# Revit family: MADEL_GRILL_AIR RETURN_FIXED BLADES 45º_DMT
name_source: partatom
category: Terminales de aire
revit_build: Autodesk Revit 2015 (Build: 20140606_1530(x64)
units: mm (PartAtom-declared; Revit-internal decimal feet)

## types (224) — shared parameters
BIMETRICAL = http://www.bimetrical.com
BIMETRICAL Category = AirTerminal
Comentarios de tipo = The DMT series grilles are designed to be used in extractors of cold and hot air. They are mounted on walls or in false ceilings.
Descripción = MADEL_Fixed blades air return grilles
Fabricante = MADEL
Family Version = 1.0
IfcExportAs = IfcAirTerminalType
IfcExportType = IfcAirTerminalType
Imagen de tipo = <Ninguno>
Material Grill = MADEL_M9016
Review Date = 11/2016
Revit Version = Revit 2015 - English
URL = http://www.madel.com
Vmax = 3.0 m/s
Vmed = 2.3 m/s
Vmin = 1.0 m/s
b_factor = -0.128138
c_factor = -8.9597
m_factor = 1.8995
n_factor = 29.792

## per-type parameters (varying)
| type | Afree | Blade Lenght | Flujo máx. | Flujo mín. | H | H1 | H2 | Height_Connector | Kf | L | L3 | Modelo | N_Graphic lines | Nº  Blades | Product Size | Width_Connector |
| DMT-AR+CM 1200x1000 | 0.1284 m² | 1179 mm | 1,387 m³/h | 462 m³/h | 1000 mm | 985 mm | 37.9 mm | 1000 mm | 1.735604 | 1200 mm | 1185 mm | DMT-AR+CM 1200x1000 | 25 | 39 | 1200x1000 | 1200 mm |
| DMT-AR+CM 1200x900 | 0.6713 m² | 1179 mm | 7,250 m³/h | 2,417 m³/h | 900 mm | 885 mm | 36.9 mm | 900 mm | 8.885922 | 1200 mm | 1185 mm | DMT-AR+CM 1200x900 | 23 | 35 | 1200x900 | 1200 mm |
| DMT-AR+CM 1200x800 | 0.5954 m² | 1179 mm | 6,431 m³/h | 2,144 m³/h | 800 mm | 785 mm | 37.4 mm | 800 mm | 8.36743 | 1200 mm | 1185 mm | DMT-AR+CM 1200x800 | 20 | 31 | 1200x800 | 1200 mm |
| DMT-AR+CM 1200x700 | 0.5196 m² | 1179 mm | 5,611 m³/h | 1,870 m³/h | 700 mm | 685 mm | 36.1 mm | 700 mm | 7.778179 | 1200 mm | 1185 mm | DMT-AR+CM 1200x700 | 18 | 27 | 1200x700 | 1200 mm |
| DMT-AR+CM 1200x600 | 0.4437 m² | 1179 mm | 4,792 m³/h | 1,597 m³/h | 600 mm | 585 mm | 36.6 mm | 600 mm | 7.095754 | 1200 mm | 1185 mm | DMT-AR+CM 1200x600 | 15 | 23 | 1200x600 | 1200 mm |
| DMT-AR+CM 1200x500 | 0.3679 m² | 1179 mm | 3,973 m³/h | 1,324 m³/h | 500 mm | 485 mm | 34.6 mm | 500 mm | 6.285056 | 1200 mm | 1185 mm | DMT-AR+CM 1200x500 | 13 | 19 | 1200x500 | 1200 mm |
| DMT-AR+CM 1200x450 | 0.3299 m² | 1179 mm | 3,563 m³/h | 1,188 m³/h | 450 mm  [stored 1.47638 ft] | 435 mm | 36.3 mm | 450 mm  [stored 1.47638 ft] | 5.814512 | 1200 mm | 1185 mm | DMT-AR+CM 1200x450 | 11 | 17 | 1200x450 | 1200 mm |
| DMT-AR+CM 1200x400 | 0.2920 m² | 1179 mm | 3,153 m³/h | 1,051 m³/h | 400 mm  [stored 1.31234 ft] | 385 mm | 35 mm  [stored 0.114829 ft] | 400 mm  [stored 1.31234 ft] | 5.286433 | 1200 mm | 1185 mm | DMT-AR+CM 1200x400 | 10 | 15 | 1200x400 | 1200 mm |
| DMT-AR+CM 1200x350 | 0.2541 m² | 1179 mm | 2,744 m³/h | 915 m³/h | 350 mm  [stored 1.14829 ft] | 335 mm | 33.5 mm | 350 mm  [stored 1.14829 ft] | 4.684763 | 1200 mm | 1185 mm | DMT-AR+CM 1200x350 | 9 | 13 | 1200x350 | 1200 mm |
| DMT-AR+CM 1200x300 | 0.2161 m² | 1179 mm | 2,334 m³/h | 778 m³/h | 300 mm | 285 mm  [stored 0.935039 ft] | 31.7 mm | 300 mm | 3.985618 | 1200 mm | 1185 mm | DMT-AR+CM 1200x300 | 8 | 11 | 1200x300 | 1200 mm |
| DMT-AR+CM 1200x250 | 0.1782 m² | 1179 mm | 1,924 m³/h | 641 m³/h | 250 mm  [stored 0.82021 ft] | 235 mm  [stored 0.770997 ft] | 33.6 mm | 250 mm  [stored 0.82021 ft] | 3.15119 | 1200 mm | 1185 mm | DMT-AR+CM 1200x250 | 6 | 9 | 1200x250 | 1200 mm |
| DMT-AR+CM 1200x200 | 0.1403 m² | 1179 mm | 1,515 m³/h | 505 m³/h | 200 mm  [stored 0.656168 ft] | 185 mm  [stored 0.606955 ft] | 30.8 mm | 200 mm  [stored 0.656168 ft] | 2.116257 | 1200 mm | 1185 mm | DMT-AR+CM 1200x200 | 5 | 7 | 1200x200 | 1200 mm |
| DMT-AR+CM 1200x150 | 0.1023 m² | 1179 mm | 1,105 m³/h | 368 m³/h | 150 mm | 135 mm  [stored 0.442913 ft] | 27 mm  [stored 0.0885827 ft] | 150 mm | 0.752929 | 1200 mm | 1185 mm | DMT-AR+CM 1200x150 | 4 | 5 | 1200x150 | 1200 mm |
| DMT-AR+CM 1200x100 | 0.0644 m² | 1179 mm | 695 m³/h | 232 m³/h | 100 mm  [stored 0.328084 ft] | 85 mm  [stored 0.278871 ft] | 21.3 mm | 100 mm  [stored 0.328084 ft] | -1.249544 | 1200 mm | 1185 mm | DMT-AR+CM 1200x100 | 3 | 3 | 1200x100 | 1200 mm |
| DMT-AR+CM 1100x1000 | 0.6841 m² | 1079 mm | 7,388 m³/h | 2,463 m³/h | 1000 mm | 985 mm | 37.9 mm | 1000 mm | 8.967505 | 1100 mm | 1085 mm | DMT-AR+CM 1100x1000 | 25 | 39 | 1100x1000 | 1100 mm |
| DMT-AR+CM 1100x900 | 0.6146 m² | 1079 mm | 6,638 m³/h | 2,213 m³/h | 900 mm | 885 mm | 36.9 mm | 900 mm | 8.504605 | 1100 mm | 1085 mm | DMT-AR+CM 1100x900 | 23 | 35 | 1100x900 | 1100 mm |
| DMT-AR+CM 1100x800 | 0.5452 m² | 1079 mm | 5,888 m³/h | 1,963 m³/h | 800 mm | 785 mm | 37.4 mm | 800 mm | 7.986136 | 1100 mm | 1085 mm | DMT-AR+CM 1100x800 | 20 | 31 | 1100x800 | 1100 mm |
| DMT-AR+CM 1100x700 | 0.4757 m² | 1079 mm | 5,138 m³/h | 1,713 m³/h | 700 mm | 685 mm | 36.1 mm | 700 mm | 7.396913 | 1100 mm | 1085 mm | DMT-AR+CM 1100x700 | 18 | 27 | 1100x700 | 1100 mm |
| DMT-AR+CM 1100x600 | 0.4063 m² | 1079 mm | 4,388 m³/h | 1,463 m³/h | 600 mm | 585 mm | 36.6 mm | 600 mm | 6.714527 | 1100 mm | 1085 mm | DMT-AR+CM 1100x600 | 15 | 23 | 1100x600 | 1100 mm |
| DMT-AR+CM 1100x500 | 0.3368 m² | 1079 mm | 3,638 m³/h | 1,213 m³/h | 500 mm | 485 mm | 34.6 mm | 500 mm | 5.903883 | 1100 mm | 1085 mm | DMT-AR+CM 1100x500 | 13 | 19 | 1100x500 | 1100 mm |
| DMT-AR+CM 1100x450 | 0.3021 m² | 1079 mm | 3,262 m³/h | 1,087 m³/h | 450 mm  [stored 1.47638 ft] | 435 mm | 36.3 mm | 450 mm  [stored 1.47638 ft] | 5.433377 | 1100 mm | 1085 mm | DMT-AR+CM 1100x450 | 11 | 17 | 1100x450 | 1100 mm |
| DMT-AR+CM 1100x400 | 0.2674 m² | 1079 mm | 2,887 m³/h | 962 m³/h | 400 mm  [stored 1.31234 ft] | 385 mm | 35 mm  [stored 0.114829 ft] | 400 mm  [stored 1.31234 ft] | 4.905344 | 1100 mm | 1085 mm | DMT-AR+CM 1100x400 | 10 | 15 | 1100x400 | 1100 mm |
| DMT-AR+CM 1100x350 | 0.2326 m² | 1079 mm | 2,512 m³/h | 837 m³/h | 350 mm  [stored 1.14829 ft] | 335 mm | 33.5 mm | 350 mm  [stored 1.14829 ft] | 4.303734 | 1100 mm | 1085 mm | DMT-AR+CM 1100x350 | 9 | 13 | 1100x350 | 1100 mm |
| DMT-AR+CM 1100x300 | 0.1979 m² | 1079 mm | 2,137 m³/h | 712 m³/h | 300 mm | 285 mm  [stored 0.935039 ft] | 31.7 mm | 300 mm | 3.60467 | 1100 mm | 1085 mm | DMT-AR+CM 1100x300 | 8 | 11 | 1100x300 | 1100 mm |
| DMT-AR+CM 1100x250 | 0.1632 m² | 1079 mm | 1,762 m³/h | 587 m³/h | 250 mm  [stored 0.82021 ft] | 235 mm  [stored 0.770997 ft] | 33.6 mm | 250 mm  [stored 0.82021 ft] | 2.770358 | 1100 mm | 1085 mm | DMT-AR+CM 1100x250 | 6 | 9 | 1100x250 | 1100 mm |
| DMT-AR+CM 1100x200 | 0.1284 m² | 1079 mm | 1,387 m³/h | 462 m³/h | 200 mm  [stored 0.656168 ft] | 185 mm  [stored 0.606955 ft] | 30.8 mm | 200 mm  [stored 0.656168 ft] | 1.735604 | 1100 mm | 1085 mm | DMT-AR+CM 1100x200 | 5 | 7 | 1100x200 | 1100 mm |
| DMT-AR+CM 1100x150 | 0.0937 m² | 1079 mm | 1,012 m³/h | 337 m³/h | 150 mm | 135 mm  [stored 0.442913 ft] | 27 mm  [stored 0.0885827 ft] | 150 mm | 0.372587 | 1100 mm | 1085 mm | DMT-AR+CM 1100x150 | 4 | 5 | 1100x150 | 1100 mm |
| DMT-AR+CM 1100x100 | 0.0590 m² | 1079 mm | 637 m³/h | 212 m³/h | 100 mm  [stored 0.328084 ft] | 85 mm  [stored 0.278871 ft] | 21.3 mm | 100 mm  [stored 0.328084 ft] | -1.629207 | 1100 mm | 1085 mm | DMT-AR+CM 1100x100 | 3 | 3 | 1100x100 | 1100 mm |
| DMT-AR+CM 1000x1000 | 0.6210 m² | 979 mm | 6,707 m³/h | 2,236 m³/h | 1000 mm | 985 mm | 37.9 mm | 1000 mm | 8.549255 | 1000 mm | 985 mm | DMT-AR+CM 1000x1000 | 25 | 39 | 1000x1000 | 1000 mm |
| DMT-AR+CM 1000x900 | 0.5580 m² | 979 mm | 6,026 m³/h | 2,009 m³/h | 900 mm | 885 mm | 36.9 mm | 900 mm | 8.086376 | 1000 mm | 985 mm | DMT-AR+CM 1000x900 | 23 | 35 | 1000x900 | 1000 mm |
| DMT-AR+CM 1000x800 | 0.4949 m² | 979 mm | 5,345 m³/h | 1,782 m³/h | 800 mm | 785 mm | 37.4 mm | 800 mm | 7.567934 | 1000 mm | 985 mm | DMT-AR+CM 1000x800 | 20 | 31 | 1000x800 | 1000 mm |
| DMT-AR+CM 1000x700 | 0.4319 m² | 979 mm | 4,664 m³/h | 1,555 m³/h | 700 mm | 685 mm | 36.1 mm | 700 mm | 6.978746 | 1000 mm | 985 mm | DMT-AR+CM 1000x700 | 18 | 27 | 1000x700 | 1000 mm |
| DMT-AR+CM 1000x600 | 0.3688 m² | 979 mm | 3,983 m³/h | 1,328 m³/h | 600 mm | 585 mm | 36.6 mm | 600 mm | 6.296407 | 1000 mm | 985 mm | DMT-AR+CM 1000x600 | 15 | 23 | 1000x600 | 1000 mm |
| DMT-AR+CM 1000x500 | 0.3058 m² | 979 mm | 3,302 m³/h | 1,101 m³/h | 500 mm | 485 mm | 34.6 mm | 500 mm | 5.485829 | 1000 mm | 985 mm | DMT-AR+CM 1000x500 | 13 | 19 | 1000x500 | 1000 mm |
| DMT-AR+CM 1000x450 | 0.2742 m² | 979 mm | 2,962 m³/h | 987 m³/h | 450 mm  [stored 1.47638 ft] | 435 mm | 36.3 mm | 450 mm  [stored 1.47638 ft] | 5.015366 | 1000 mm | 985 mm | DMT-AR+CM 1000x450 | 11 | 17 | 1000x450 | 1000 mm |
| DMT-AR+CM 1000x400 | 0.2427 m² | 979 mm | 2,621 m³/h | 874 m³/h | 400 mm  [stored 1.31234 ft] | 385 mm | 35 mm  [stored 0.114829 ft] | 400 mm  [stored 1.31234 ft] | 4.48739 | 1000 mm | 985 mm | DMT-AR+CM 1000x400 | 10 | 15 | 1000x400 | 1000 mm |
| DMT-AR+CM 1000x350 | 0.2112 m² | 979 mm | 2,281 m³/h | 760 m³/h | 350 mm  [stored 1.14829 ft] | 335 mm | 33.5 mm | 350 mm  [stored 1.14829 ft] | 3.885852 | 1000 mm | 985 mm | DMT-AR+CM 1000x350 | 9 | 13 | 1000x350 | 1000 mm |
| DMT-AR+CM 1000x300 | 0.1797 m² | 979 mm | 1,940 m³/h | 647 m³/h | 300 mm | 285 mm  [stored 0.935039 ft] | 31.7 mm | 300 mm | 3.186886 | 1000 mm | 985 mm | DMT-AR+CM 1000x300 | 8 | 11 | 1000x300 | 1000 mm |
| DMT-AR+CM 1000x250 | 0.1481 m² | 979 mm | 1,600 m³/h | 533 m³/h | 250 mm  [stored 0.82021 ft] | 235 mm  [stored 0.770997 ft] | 33.6 mm | 250 mm  [stored 0.82021 ft] | 2.352714 | 1000 mm | 985 mm | DMT-AR+CM 1000x250 | 6 | 9 | 1000x250 | 1000 mm |
| DMT-AR+CM 1000x200 | 0.1166 m² | 979 mm | 1,259 m³/h | 420 m³/h | 200 mm  [stored 0.656168 ft] | 185 mm  [stored 0.606955 ft] | 30.8 mm | 200 mm  [stored 0.656168 ft] | 1.318174 | 1000 mm | 985 mm | DMT-AR+CM 1000x200 | 5 | 7 | 1000x200 | 1000 mm |
| DMT-AR+CM 1000x150 | 0.0851 m² | 979 mm | 919 m³/h | 306 m³/h | 150 mm | 135 mm  [stored 0.442913 ft] | 27 mm  [stored 0.0885827 ft] | 150 mm | -0.044469 | 1000 mm | 985 mm | DMT-AR+CM 1000x150 | 4 | 5 | 1000x150 | 1000 mm |
| DMT-AR+CM 1000x100 | 0.0536 m² | 979 mm | 579 m³/h | 193 m³/h | 100 mm  [stored 0.328084 ft] | 85 mm  [stored 0.278871 ft] | 21.3 mm | 100 mm  [stored 0.328084 ft] | -2.045448 | 1000 mm | 985 mm | DMT-AR+CM 1000x100 | 3 | 3 | 1000x100 | 1000 mm |
| EMT-AR+CM 1000x900 | 0.5579 m² | 879 mm | 6,026 m³/h | 2,009 m³/h | 1000 mm | 985 mm | 37.9 mm | 1000 mm | 8.086169 | 900 mm | 885 mm | EMT-AR+CM 1000x900 | 25 | 39 | 900x1000 | 900 mm |
| DMT-AR+CM 900x900 | 0.5013 m² | 879 mm | 5,414 m³/h | 1,805 m³/h | 900 mm | 885 mm | 36.9 mm | 900 mm | 7.623316 | 900 mm | 885 mm | DMT-AR+CM 900x900 | 23 | 35 | 900x900 | 900 mm |
| DMT-AR+CM 900x800 | 0.4447 m² | 879 mm | 4,802 m³/h | 1,601 m³/h | 800 mm | 785 mm | 37.4 mm | 800 mm | 7.104907 | 900 mm | 885 mm | DMT-AR+CM 900x800 | 20 | 31 | 900x800 | 900 mm |
| DMT-AR+CM 900x700 | 0.3880 m² | 879 mm | 4,191 m³/h | 1,397 m³/h | 700 mm | 685 mm | 36.1 mm | 700 mm | 6.515761 | 900 mm | 885 mm | DMT-AR+CM 900x700 | 18 | 27 | 900x700 | 900 mm |
| DMT-AR+CM 900x600 | 0.3314 m² | 879 mm | 3,579 m³/h | 1,193 m³/h | 600 mm | 585 mm | 36.6 mm | 600 mm | 5.833479 | 900 mm | 885 mm | DMT-AR+CM 900x600 | 15 | 23 | 900x600 | 900 mm |
| DMT-AR+CM 900x500 | 0.2747 m² | 879 mm | 2,967 m³/h | 989 m³/h | 500 mm | 485 mm | 34.6 mm | 500 mm | 5.022982 | 900 mm | 885 mm | DMT-AR+CM 900x500 | 13 | 19 | 900x500 | 900 mm |
| DMT-AR+CM 900x450 | 0.2464 m² | 879 mm | 2,661 m³/h | 887 m³/h | 450 mm  [stored 1.47638 ft] | 435 mm | 36.3 mm | 450 mm  [stored 1.47638 ft] | 4.552574 | 900 mm | 885 mm | DMT-AR+CM 900x450 | 11 | 17 | 900x450 | 900 mm |
| DMT-AR+CM 900x400 | 0.2181 m² | 879 mm | 2,355 m³/h | 785 m³/h | 400 mm  [stored 1.31234 ft] | 385 mm | 35 mm  [stored 0.114829 ft] | 400 mm  [stored 1.31234 ft] | 4.024666 | 900 mm | 885 mm | DMT-AR+CM 900x400 | 10 | 15 | 900x400 | 900 mm |
| DMT-AR+CM 900x350 | 0.1898 m² | 879 mm | 2,049 m³/h | 683 m³/h | 350 mm  [stored 1.14829 ft] | 335 mm | 33.5 mm | 350 mm  [stored 1.14829 ft] | 3.423217 | 900 mm | 885 mm | DMT-AR+CM 900x350 | 9 | 13 | 900x350 | 900 mm |
| DMT-AR+CM 900x300 | 0.1614 m² | 879 mm | 1,744 m³/h | 581 m³/h | 300 mm | 285 mm  [stored 0.935039 ft] | 31.7 mm | 300 mm | 2.724371 | 900 mm | 885 mm | DMT-AR+CM 900x300 | 8 | 11 | 900x300 | 900 mm |
| DMT-AR+CM 900x250 | 0.1331 m² | 879 mm | 1,438 m³/h | 479 m³/h | 250 mm  [stored 0.82021 ft] | 235 mm  [stored 0.770997 ft] | 33.6 mm | 250 mm  [stored 0.82021 ft] | 1.89037 | 900 mm | 885 mm | DMT-AR+CM 900x250 | 6 | 9 | 900x250 | 900 mm |
| DMT-AR+CM 900x200 | 0.1048 m² | 879 mm | 1,132 m³/h | 377 m³/h | 200 mm  [stored 0.656168 ft] | 185 mm  [stored 0.606955 ft] | 30.8 mm | 200 mm  [stored 0.656168 ft] | 0.856094 | 900 mm | 885 mm | DMT-AR+CM 900x200 | 5 | 7 | 900x200 | 900 mm |
| DMT-AR+CM 900x150 | 0.0765 m² | 879 mm | 826 m³/h | 275 m³/h | 150 mm | 135 mm  [stored 0.442913 ft] | 27 mm  [stored 0.0885827 ft] | 150 mm | -0.50609 | 900 mm | 885 mm | DMT-AR+CM 900x150 | 4 | 5 | 900x150 | 900 mm |
| DMT-AR+CM 900x100 | 0.0482 m² | 879 mm | 520 m³/h | 173 m³/h | 100 mm  [stored 0.328084 ft] | 85 mm  [stored 0.278871 ft] | 21.3 mm | 100 mm  [stored 0.328084 ft] | -2.506071 | 900 mm | 885 mm | DMT-AR+CM 900x100 | 3 | 3 | 900x100 | 900 mm |
| EMT-AR+CM 1000x800 | 0.4949 m² | 779 mm | 5,345 m³/h | 1,782 m³/h | 1000 mm | 985 mm | 37.9 mm | 1000 mm | 7.567467 | 800 mm | 785 mm | EMT-AR+CM 1000x800 | 25 | 39 | 800x1000 | 800 mm |
| EMT-AR+CM 900x800 | 0.4446 m² | 779 mm | 4,802 m³/h | 1,601 m³/h | 900 mm | 885 mm | 36.9 mm | 900 mm | 7.104647 | 800 mm | 785 mm | EMT-AR+CM 900x800 | 23 | 35 | 800x900 | 800 mm |
| DMT-AR+CM 800x800 | 0.3944 m² | 779 mm | 4,259 m³/h | 1,420 m³/h | 800 mm | 785 mm | 37.4 mm | 800 mm | 6.586279 | 800 mm | 785 mm | DMT-AR+CM 800x800 | 20 | 31 | 800x800 | 800 mm |
| DMT-AR+CM 800x700 | 0.3442 m² | 779 mm | 3,717 m³/h | 1,239 m³/h | 700 mm | 685 mm | 36.1 mm | 700 mm | 5.997187 | 800 mm | 785 mm | DMT-AR+CM 800x700 | 18 | 27 | 800x700 | 800 mm |
| DMT-AR+CM 800x600 | 0.2939 m² | 779 mm | 3,174 m³/h | 1,058 m³/h | 600 mm | 585 mm | 36.6 mm | 600 mm | 5.314977 | 800 mm | 785 mm | DMT-AR+CM 800x600 | 15 | 23 | 800x600 | 800 mm |
| DMT-AR+CM 800x500 | 0.2437 m² | 779 mm | 2,632 m³/h | 877 m³/h | 500 mm | 485 mm | 34.6 mm | 500 mm | 4.504581 | 800 mm | 785 mm | DMT-AR+CM 800x500 | 13 | 19 | 800x500 | 800 mm |
| DMT-AR+CM 800x450 | 0.2186 m² | 779 mm | 2,361 m³/h | 787 m³/h | 450 mm  [stored 1.47638 ft] | 435 mm | 36.3 mm | 450 mm  [stored 1.47638 ft] | 4.034241 | 800 mm | 785 mm | DMT-AR+CM 800x450 | 11 | 17 | 800x450 | 800 mm |
| DMT-AR+CM 800x400 | 0.1934 m² | 779 mm | 2,089 m³/h | 696 m³/h | 400 mm  [stored 1.31234 ft] | 385 mm | 35 mm  [stored 0.114829 ft] | 400 mm  [stored 1.31234 ft] | 3.506418 | 800 mm | 785 mm | DMT-AR+CM 800x400 | 10 | 15 | 800x400 | 800 mm |
| DMT-AR+CM 800x350 | 0.1683 m² | 779 mm | 1,818 m³/h | 606 m³/h | 350 mm  [stored 1.14829 ft] | 335 mm | 33.5 mm | 350 mm  [stored 1.14829 ft] | 2.905081 | 800 mm | 785 mm | DMT-AR+CM 800x350 | 9 | 13 | 800x350 | 800 mm |
| DMT-AR+CM 800x300 | 0.1432 m² | 779 mm | 1,547 m³/h | 516 m³/h | 300 mm | 285 mm  [stored 0.935039 ft] | 31.7 mm | 300 mm | 2.206385 | 800 mm | 785 mm | DMT-AR+CM 800x300 | 8 | 11 | 800x300 | 800 mm |
| DMT-AR+CM 800x250 | 0.1181 m² | 779 mm | 1,275 m³/h | 425 m³/h | 250 mm  [stored 0.82021 ft] | 235 mm  [stored 0.770997 ft] | 33.6 mm | 250 mm  [stored 0.82021 ft] | 1.372599 | 800 mm | 785 mm | DMT-AR+CM 800x250 | 6 | 9 | 800x250 | 800 mm |
| DMT-AR+CM 800x200 | 0.0930 m² | 779 mm | 1,004 m³/h | 335 m³/h | 200 mm  [stored 0.656168 ft] | 185 mm  [stored 0.606955 ft] | 30.8 mm | 200 mm  [stored 0.656168 ft] | 0.338653 | 800 mm | 785 mm | DMT-AR+CM 800x200 | 5 | 7 | 800x200 | 800 mm |
| DMT-AR+CM 800x150 | 0.0679 m² | 779 mm | 733 m³/h | 244 m³/h | 150 mm | 135 mm  [stored 0.442913 ft] | 27 mm  [stored 0.0885827 ft] | 150 mm | -1.022955 | 800 mm | 785 mm | DMT-AR+CM 800x150 | 4 | 5 | 800x150 | 800 mm |
| DMT-AR+CM 800x100 | 0.0427 m² | 779 mm | 462 m³/h | 154 m³/h | 100 mm  [stored 0.328084 ft] | 85 mm  [stored 0.278871 ft] | 21.3 mm | 100 mm  [stored 0.328084 ft] | -3.021685 | 800 mm | 785 mm | DMT-AR+CM 800x100 | 3 | 3 | 800x100 | 800 mm |
| EMT-AR+CM 1000x700 | 0.4318 m² | 679 mm | 4,663 m³/h | 1,554 m³/h | 1000 mm | 985 mm | 37.9 mm | 1000 mm | 6.977943 | 700 mm | 685 mm | EMT-AR+CM 1000x700 | 25 | 39 | 700x1000 | 700 mm |
| EMT-AR+CM 900x700 | 0.3880 m² | 679 mm | 4,190 m³/h | 1,397 m³/h | 900 mm | 885 mm | 36.9 mm | 900 mm | 6.515166 | 700 mm | 685 mm | EMT-AR+CM 900x700 | 23 | 35 | 700x900 | 700 mm |
| EMT-AR+CM 800x700 | 0.3441 m² | 679 mm | 3,717 m³/h | 1,239 m³/h | 800 mm | 785 mm | 37.4 mm | 800 mm | 5.996851 | 700 mm | 685 mm | EMT-AR+CM 800x700 | 20 | 31 | 700x800 | 700 mm |
| DMT-AR+CM 700x700 | 0.3003 m² | 679 mm | 3,243 m³/h | 1,081 m³/h | 700 mm | 685 mm | 36.1 mm | 700 mm | 5.407828 | 700 mm | 685 mm | DMT-AR+CM 700x700 | 18 | 27 | 700x700 | 700 mm |
| DMT-AR+CM 700x600 | 0.2565 m² | 679 mm | 2,770 m³/h | 923 m³/h | 600 mm | 585 mm | 36.6 mm | 600 mm | 4.725711 | 700 mm | 685 mm | DMT-AR+CM 700x600 | 15 | 23 | 700x600 | 700 mm |
| DMT-AR+CM 700x500 | 0.2126 m² | 679 mm | 2,297 m³/h | 766 m³/h | 500 mm | 485 mm | 34.6 mm | 500 mm | 3.915446 | 700 mm | 685 mm | DMT-AR+CM 700x500 | 13 | 19 | 700x500 | 700 mm |
| DMT-AR+CM 700x450 | 0.1907 m² | 679 mm | 2,060 m³/h | 687 m³/h | 450 mm  [stored 1.47638 ft] | 435 mm | 36.3 mm | 450 mm  [stored 1.47638 ft] | 3.445194 | 700 mm | 685 mm | DMT-AR+CM 700x450 | 11 | 17 | 700x450 | 700 mm |
| DMT-AR+CM 700x400 | 0.1688 m² | 679 mm | 1,823 m³/h | 608 m³/h | 400 mm  [stored 1.31234 ft] | 385 mm | 35 mm  [stored 0.114829 ft] | 400 mm  [stored 1.31234 ft] | 2.917482 | 700 mm | 685 mm | DMT-AR+CM 700x400 | 10 | 15 | 700x400 | 700 mm |
| DMT-AR+CM 700x350 | 0.1469 m² | 679 mm | 1,587 m³/h | 529 m³/h | 350 mm  [stored 1.14829 ft] | 335 mm | 33.5 mm | 350 mm  [stored 1.14829 ft] | 2.316289 | 700 mm | 685 mm | DMT-AR+CM 700x350 | 9 | 13 | 700x350 | 700 mm |
| DMT-AR+CM 700x300 | 0.1250 m² | 679 mm | 1,350 m³/h | 450 m³/h | 300 mm | 285 mm  [stored 0.935039 ft] | 31.7 mm | 300 mm | 1.617787 | 700 mm | 685 mm | DMT-AR+CM 700x300 | 8 | 11 | 700x300 | 700 mm |
| DMT-AR+CM 700x250 | 0.1031 m² | 679 mm | 1,113 m³/h | 371 m³/h | 250 mm  [stored 0.82021 ft] | 235 mm  [stored 0.770997 ft] | 33.6 mm | 250 mm  [stored 0.82021 ft] | 0.784278 | 700 mm | 685 mm | DMT-AR+CM 700x250 | 6 | 9 | 700x250 | 700 mm |
| DMT-AR+CM 700x200 | 0.0812 m² | 679 mm | 876 m³/h | 292 m³/h | 200 mm  [stored 0.656168 ft] | 185 mm  [stored 0.606955 ft] | 30.8 mm | 200 mm  [stored 0.656168 ft] | -0.24924 | 700 mm | 685 mm | DMT-AR+CM 700x200 | 5 | 7 | 700x200 | 700 mm |
| DMT-AR+CM 700x150 | 0.0592 m² | 679 mm | 640 m³/h | 213 m³/h | 150 mm | 135 mm  [stored 0.442913 ft] | 27 mm  [stored 0.0885827 ft] | 150 mm | -1.610107 | 700 mm | 685 mm | DMT-AR+CM 700x150 | 4 | 5 | 700x150 | 700 mm |
| DMT-AR+CM 700x100 | 0.0373 m² | 679 mm | 403 m³/h | 134 m³/h | 100 mm  [stored 0.328084 ft] | 85 mm  [stored 0.278871 ft] | 21.3 mm | 100 mm  [stored 0.328084 ft] | -3.607221 | 700 mm | 685 mm | DMT-AR+CM 700x100 | 3 | 3 | 700x100 | 700 mm |
| EMT-AR+CM 1000x600 | 0.3687 m² | 579 mm | 3,982 m³/h | 1,327 m³/h | 1000 mm | 985 mm | 37.9 mm | 1000 mm | 6.295153 | 600 mm | 585 mm | EMT-AR+CM 1000x600 | 25 | 39 | 600x1000 | 600 mm |
| EMT-AR+CM 900x600 | 0.3313 m² | 579 mm | 3,578 m³/h | 1,193 m³/h | 900 mm | 885 mm | 36.9 mm | 900 mm | 5.832433 | 600 mm | 585 mm | EMT-AR+CM 900x600 | 23 | 35 | 600x900 | 600 mm |
| EMT-AR+CM 800x600 | 0.2939 m² | 579 mm | 3,174 m³/h | 1,058 m³/h | 800 mm | 785 mm | 37.4 mm | 800 mm | 5.31419 | 600 mm | 585 mm | EMT-AR+CM 800x600 | 20 | 31 | 600x800 | 600 mm |
| EMT-AR+CM 700x600 | 0.2564 m² | 579 mm | 2,770 m³/h | 923 m³/h | 700 mm | 685 mm | 36.1 mm | 700 mm | 4.72526 | 600 mm | 585 mm | EMT-AR+CM 700x600 | 18 | 27 | 600x700 | 600 mm |
| DMT-AR+CM 600x600 | 0.2190 m² | 579 mm | 2,365 m³/h | 788 m³/h | 600 mm | 585 mm | 36.6 mm | 600 mm | 4.043267 | 600 mm | 585 mm | DMT-AR+CM 600x600 | 15 | 23 | 600x600 | 600 mm |
| DMT-AR+CM 600x500 | 0.1816 m² | 579 mm | 1,961 m³/h | 654 m³/h | 500 mm | 485 mm | 34.6 mm | 500 mm | 3.233178 | 600 mm | 585 mm | DMT-AR+CM 600x500 | 13 | 19 | 600x500 | 600 mm |
| DMT-AR+CM 600x450 | 0.1629 m² | 579 mm | 1,759 m³/h | 586 m³/h | 450 mm  [stored 1.47638 ft] | 435 mm | 36.3 mm | 450 mm  [stored 1.47638 ft] | 2.763044 | 600 mm | 585 mm | DMT-AR+CM 600x450 | 11 | 17 | 600x450 | 600 mm |
| DMT-AR+CM 600x400 | 0.1442 m² | 579 mm | 1,557 m³/h | 519 m³/h | 400 mm  [stored 1.31234 ft] | 385 mm | 35 mm  [stored 0.114829 ft] | 400 mm  [stored 1.31234 ft] | 2.235481 | 600 mm | 585 mm | DMT-AR+CM 600x400 | 10 | 15 | 600x400 | 600 mm |
| DMT-AR+CM 600x350 | 0.1255 m² | 579 mm | 1,355 m³/h | 452 m³/h | 350 mm  [stored 1.14829 ft] | 335 mm | 33.5 mm | 350 mm  [stored 1.14829 ft] | 1.634481 | 600 mm | 585 mm | DMT-AR+CM 600x350 | 9 | 13 | 600x350 | 600 mm |
| DMT-AR+CM 600x300 | 0.1068 m² | 579 mm | 1,153 m³/h | 384 m³/h | 300 mm | 285 mm  [stored 0.935039 ft] | 31.7 mm | 300 mm | 0.93624 | 600 mm | 585 mm | DMT-AR+CM 600x300 | 8 | 11 | 600x300 | 600 mm |
| DMT-AR+CM 600x250 | 0.0880 m² | 579 mm | 951 m³/h | 317 m³/h | 250 mm  [stored 0.82021 ft] | 235 mm  [stored 0.770997 ft] | 33.6 mm | 250 mm  [stored 0.82021 ft] | 0.103103 | 600 mm | 585 mm | DMT-AR+CM 600x250 | 6 | 9 | 600x250 | 600 mm |
| DMT-AR+CM 600x200 | 0.0693 m² | 579 mm | 749 m³/h | 250 m³/h | 200 mm  [stored 0.656168 ft] | 185 mm  [stored 0.606955 ft] | 30.8 mm | 200 mm  [stored 0.656168 ft] | -0.929843 | 600 mm | 585 mm | DMT-AR+CM 600x200 | 5 | 7 | 600x200 | 600 mm |
| DMT-AR+CM 600x150 | 0.0506 m² | 579 mm | 547 m³/h | 182 m³/h | 150 mm | 135 mm  [stored 0.442913 ft] | 27 mm  [stored 0.0885827 ft] | 150 mm | -2.289714 | 600 mm | 585 mm | DMT-AR+CM 600x150 | 4 | 5 | 600x150 | 600 mm |
| DMT-AR+CM 600x100 | 0.0319 m² | 579 mm | 345 m³/h | 115 m³/h | 100 mm  [stored 0.328084 ft] | 85 mm  [stored 0.278871 ft] | 21.3 mm | 100 mm  [stored 0.328084 ft] | -4.284664 | 600 mm | 585 mm | DMT-AR+CM 600x100 | 3 | 3 | 600x100 | 600 mm |
| EMT-AR+CM 1000x500 | 0.3056 m² | 479 mm  [stored 1.57152 ft] | 3,301 m³/h | 1,100 m³/h | 1000 mm | 985 mm | 37.9 mm | 1000 mm | 5.483939 | 500 mm | 485 mm | EMT-AR+CM 1000x500 | 25 | 39 | 500x1000 | 500 mm |
| EMT-AR+CM 900x500 | 0.2746 m² | 479 mm  [stored 1.57152 ft] | 2,966 m³/h | 989 m³/h | 900 mm | 885 mm | 36.9 mm | 900 mm | 5.0213 | 500 mm | 485 mm | EMT-AR+CM 900x500 | 23 | 35 | 500x900 | 500 mm |
| EMT-AR+CM 800x500 | 0.2436 m² | 479 mm  [stored 1.57152 ft] | 2,631 m³/h | 877 m³/h | 800 mm | 785 mm | 37.4 mm | 800 mm | 4.503158 | 500 mm | 485 mm | EMT-AR+CM 800x500 | 20 | 31 | 500x800 | 500 mm |
| EMT-AR+CM 700x500 | 0.2126 m² | 479 mm  [stored 1.57152 ft] | 2,296 m³/h | 765 m³/h | 700 mm | 685 mm | 36.1 mm | 700 mm | 3.914359 | 500 mm | 485 mm | EMT-AR+CM 700x500 | 18 | 27 | 500x700 | 500 mm |
| EMT-AR+CM 600x500 | 0.1816 m² | 479 mm  [stored 1.57152 ft] | 1,961 m³/h | 654 m³/h | 600 mm | 585 mm | 36.6 mm | 600 mm | 3.232542 | 500 mm | 485 mm | EMT-AR+CM 600x500 | 15 | 23 | 500x600 | 500 mm |
| DMT-AR+CM 500x500 | 0.1506 m² | 479 mm  [stored 1.57152 ft] | 1,626 m³/h | 542 m³/h | 500 mm | 485 mm | 34.6 mm | 500 mm | 2.4227 | 500 mm | 485 mm | DMT-AR+CM 500x500 | 13 | 19 | 500x500 | 500 mm |
| DMT-AR+CM 500x450 | 0.1351 m² | 479 mm  [stored 1.57152 ft] | 1,459 m³/h | 486 m³/h | 450 mm  [stored 1.47638 ft] | 435 mm | 36.3 mm | 450 mm  [stored 1.47638 ft] | 1.952733 | 500 mm | 485 mm | DMT-AR+CM 500x450 | 11 | 17 | 500x450 | 500 mm |
| DMT-AR+CM 500x400 | 0.1195 m² | 479 mm  [stored 1.57152 ft] | 1,291 m³/h | 430 m³/h | 400 mm  [stored 1.31234 ft] | 385 mm | 35 mm  [stored 0.114829 ft] | 400 mm  [stored 1.31234 ft] | 1.42538 | 500 mm | 485 mm | DMT-AR+CM 500x400 | 10 | 15 | 500x400 | 500 mm |
| DMT-AR+CM 500x350 | 0.1040 m² | 479 mm  [stored 1.57152 ft] | 1,124 m³/h | 375 m³/h | 350 mm  [stored 1.14829 ft] | 335 mm | 33.5 mm | 350 mm  [stored 1.14829 ft] | 0.824653 | 500 mm | 485 mm | DMT-AR+CM 500x350 | 9 | 13 | 500x350 | 500 mm |
| DMT-AR+CM 500x300 | 0.0885 m² | 479 mm  [stored 1.57152 ft] | 956 m³/h | 319 m³/h | 300 mm | 285 mm  [stored 0.935039 ft] | 31.7 mm | 300 mm | 0.126781 | 500 mm | 485 mm | DMT-AR+CM 500x300 | 8 | 11 | 500x300 | 500 mm |
| DMT-AR+CM 500x250 | 0.0730 m² | 479 mm  [stored 1.57152 ft] | 789 m³/h | 263 m³/h | 250 mm  [stored 0.82021 ft] | 235 mm  [stored 0.770997 ft] | 33.6 mm | 250 mm  [stored 0.82021 ft] | -0.705832 | 500 mm | 485 mm | DMT-AR+CM 500x250 | 6 | 9 | 500x250 | 500 mm |
| DMT-AR+CM 500x200 | 0.0575 m² | 479 mm  [stored 1.57152 ft] | 621 m³/h | 207 m³/h | 200 mm  [stored 0.656168 ft] | 185 mm  [stored 0.606955 ft] | 30.8 mm | 200 mm  [stored 0.656168 ft] | -1.73797 | 500 mm | 485 mm | DMT-AR+CM 500x200 | 5 | 7 | 500x200 | 500 mm |
| DMT-AR+CM 500x150 | 0.0420 m² | 479 mm  [stored 1.57152 ft] | 454 m³/h | 151 m³/h | 150 mm | 135 mm  [stored 0.442913 ft] | 27 mm  [stored 0.0885827 ft] | 150 mm | -3.096436 | 500 mm | 485 mm | DMT-AR+CM 500x150 | 4 | 5 | 500x150 | 500 mm |
| DMT-AR+CM 500x100 | 0.0265 m² | 479 mm  [stored 1.57152 ft] | 286 m³/h | 95 m³/h | 100 mm  [stored 0.328084 ft] | 85 mm  [stored 0.278871 ft] | 21.3 mm | 100 mm  [stored 0.328084 ft] | -5.088336 | 500 mm | 485 mm | DMT-AR+CM 500x100 | 3 | 3 | 500x100 | 500 mm |
| EMT-AR+CM 1000x450 | 0.2741 m² | 429 mm | 2,960 m³/h | 987 m³/h | 1000 mm | 985 mm | 37.9 mm | 1000 mm | 5.013048 | 450 mm  [stored 1.47638 ft] | 435 mm | EMT-AR+CM 1000x450 | 25 | 39 | 450x1000 | 450 mm  [stored 1.47638 ft] |
| EMT-AR+CM 900x450 | 0.2463 m² | 429 mm | 2,660 m³/h | 887 m³/h | 900 mm | 885 mm | 36.9 mm | 900 mm | 4.550463 | 450 mm  [stored 1.47638 ft] | 435 mm | EMT-AR+CM 900x450 | 23 | 35 | 450x900 | 450 mm  [stored 1.47638 ft] |
| EMT-AR+CM 800x450 | 0.2185 m² | 429 mm | 2,360 m³/h | 787 m³/h | 800 mm | 785 mm | 37.4 mm | 800 mm | 4.03239 | 450 mm  [stored 1.47638 ft] | 435 mm | EMT-AR+CM 800x450 | 20 | 31 | 450x800 | 450 mm  [stored 1.47638 ft] |
| EMT-AR+CM 700x450 | 0.1907 m² | 429 mm | 2,059 m³/h | 686 m³/h | 700 mm | 685 mm | 36.1 mm | 700 mm | 3.443679 | 450 mm  [stored 1.47638 ft] | 435 mm | EMT-AR+CM 700x450 | 18 | 27 | 450x700 | 450 mm  [stored 1.47638 ft] |
| EMT-AR+CM 600x450 | 0.1628 m² | 429 mm | 1,759 m³/h | 586 m³/h | 600 mm | 585 mm | 36.6 mm | 600 mm | 2.76198 | 450 mm  [stored 1.47638 ft] | 435 mm | EMT-AR+CM 600x450 | 15 | 23 | 450x600 | 450 mm  [stored 1.47638 ft] |
| EMT-AR+CM 500x450 | 0.1350 m² | 429 mm | 1,458 m³/h | 486 m³/h | 500 mm | 485 mm | 34.6 mm | 500 mm | 1.952305 | 450 mm  [stored 1.47638 ft] | 435 mm | DMT-AR+CM 450x500 | 13 | 19 | 450x500 | 450 mm  [stored 1.47638 ft] |
| DMT-AR+CM 450x450 | 0.1211 m² | 429 mm | 1,308 m³/h | 436 m³/h | 450 mm  [stored 1.47638 ft] | 435 mm | 36.3 mm | 450 mm  [stored 1.47638 ft] | 1.48245 | 450 mm  [stored 1.47638 ft] | 435 mm | DMT-AR+CM 450x450 | 11 | 17 | 450x450 | 450 mm  [stored 1.47638 ft] |
| DMT-AR+CM 450x400 | 0.1072 m² | 429 mm | 1,158 m³/h | 386 m³/h | 400 mm  [stored 1.31234 ft] | 385 mm | 35 mm  [stored 0.114829 ft] | 400 mm  [stored 1.31234 ft] | 0.955239 | 450 mm  [stored 1.47638 ft] | 435 mm | DMT-AR+CM 450x400 | 10 | 15 | 450x400 | 450 mm  [stored 1.47638 ft] |
| DMT-AR+CM 450x350 | 0.0933 m² | 429 mm | 1,008 m³/h | 336 m³/h | 350 mm  [stored 1.14829 ft] | 335 mm | 33.5 mm | 350 mm  [stored 1.14829 ft] | 0.354695 | 450 mm  [stored 1.47638 ft] | 435 mm | DMT-AR+CM 450x350 | 9 | 13 | 450x350 | 450 mm  [stored 1.47638 ft] |
| DMT-AR+CM 450x300 | 0.0794 m² | 429 mm | 858 m³/h | 286 m³/h | 300 mm | 285 mm  [stored 0.935039 ft] | 31.7 mm | 300 mm | -0.34293 | 450 mm  [stored 1.47638 ft] | 435 mm | DMT-AR+CM 450x300 | 8 | 11 | 450x300 | 450 mm  [stored 1.47638 ft] |
| DMT-AR+CM 450x250 | 0.0655 m² | 429 mm | 708 m³/h | 236 m³/h | 250 mm  [stored 0.82021 ft] | 235 mm  [stored 0.770997 ft] | 33.6 mm | 250 mm  [stored 0.82021 ft] | -1.17519 | 450 mm  [stored 1.47638 ft] | 435 mm | DMT-AR+CM 450x250 | 6 | 9 | 450x250 | 450 mm  [stored 1.47638 ft] |
| DMT-AR+CM 450x200 | 0.0516 m² | 429 mm | 557 m³/h | 186 m³/h | 200 mm  [stored 0.656168 ft] | 185 mm  [stored 0.606955 ft] | 30.8 mm | 200 mm  [stored 0.656168 ft] | -2.206786 | 450 mm  [stored 1.47638 ft] | 435 mm | DMT-AR+CM 450x200 | 5 | 7 | 450x200 | 450 mm  [stored 1.47638 ft] |
| DMT-AR+CM 450x150 | 0.0377 m² | 429 mm | 407 m³/h | 136 m³/h | 150 mm | 135 mm  [stored 0.442913 ft] | 27 mm  [stored 0.0885827 ft] | 150 mm | -3.564308 | 450 mm  [stored 1.47638 ft] | 435 mm | DMT-AR+CM 450x150 | 4 | 5 | 450x150 | 450 mm  [stored 1.47638 ft] |
| DMT-AR+CM 450x100 | 0.0238 m² | 429 mm | 257 m³/h | 86 m³/h | 100 mm  [stored 0.328084 ft] | 85 mm  [stored 0.278871 ft] | 21.3 mm | 100 mm  [stored 0.328084 ft] | -5.554161 | 450 mm  [stored 1.47638 ft] | 435 mm | DMT-AR+CM 450x100 | 3 | 3 | 450x100 | 450 mm  [stored 1.47638 ft] |
| EMT-AR+CM 1000x400 | 0.2426 m² | 379 mm | 2,620 m³/h | 873 m³/h | 1000 mm | 985 mm | 37.9 mm | 1000 mm | 4.484532 | 400 mm  [stored 1.31234 ft] | 385 mm | EMT-AR+CM 1000x400 | 25 | 39 | 400x1000 | 400 mm  [stored 1.31234 ft] |
| EMT-AR+CM 900x400 | 0.2179 m² | 379 mm | 2,354 m³/h | 785 m³/h | 900 mm | 885 mm | 36.9 mm | 900 mm | 4.022016 | 400 mm  [stored 1.31234 ft] | 385 mm | DMT-AR+CM 400x900 | 23 | 35 | 400x900 | 400 mm  [stored 1.31234 ft] |
| EMT-AR+CM 800x400 | 0.1933 m² | 379 mm | 2,088 m³/h | 696 m³/h | 800 mm | 785 mm | 37.4 mm | 800 mm | 3.504029 | 400 mm  [stored 1.31234 ft] | 385 mm | EMT-AR+CM 800x400 | 20 | 31 | 400x800 | 400 mm  [stored 1.31234 ft] |
| EMT-AR+CM 700x400 | 0.1687 m² | 379 mm | 1,822 m³/h | 607 m³/h | 700 mm | 685 mm | 36.1 mm | 700 mm | 2.915428 | 400 mm  [stored 1.31234 ft] | 385 mm | EMT-AR+CM 700x400 | 18 | 27 | 400x700 | 400 mm  [stored 1.31234 ft] |
| EMT-AR+CM 600x400 | 0.1441 m² | 379 mm | 1,557 m³/h | 519 m³/h | 600 mm | 585 mm | 36.6 mm | 600 mm | 2.233878 | 400 mm  [stored 1.31234 ft] | 385 mm | EMT-AR+CM 600x400 | 15 | 23 | 400x600 | 400 mm  [stored 1.31234 ft] |
| EMT-AR+CM 500x400 | 0.1195 m² | 379 mm | 1,291 m³/h | 430 m³/h | 500 mm | 485 mm | 34.6 mm | 500 mm | 1.424414 | 400 mm  [stored 1.31234 ft] | 385 mm | EMT-AR+CM 500x400 | 13 | 19 | 400x500 | 400 mm  [stored 1.31234 ft] |
| EMT-AR+CM 450x400 | 0.1072 m² | 379 mm | 1,158 m³/h | 386 m³/h | 450 mm  [stored 1.47638 ft] | 435 mm | 36.3 mm | 450 mm  [stored 1.47638 ft] | 0.9547 | 400 mm  [stored 1.31234 ft] | 385 mm | EMT-AR+CM 450x400 | 11 | 17 | 400x450 | 400 mm  [stored 1.31234 ft] |
| DMT-AR+CM 400x400 | 0.0949 m² | 379 mm | 1,025 m³/h | 342 m³/h | 400 mm  [stored 1.31234 ft] | 385 mm | 35 mm  [stored 0.114829 ft] | 400 mm  [stored 1.31234 ft] | 0.427666 | 400 mm  [stored 1.31234 ft] | 385 mm | DMT-AR+CM 400x400 | 10 | 15 | 400x400 | 400 mm  [stored 1.31234 ft] |
| DMT-AR+CM 400x350 | 0.0826 m² | 379 mm | 892 m³/h | 297 m³/h | 350 mm  [stored 1.14829 ft] | 335 mm | 33.5 mm | 350 mm  [stored 1.14829 ft] | -0.172647 | 400 mm  [stored 1.31234 ft] | 385 mm | DMT-AR+CM 400x350 | 9 | 13 | 400x350 | 400 mm  [stored 1.31234 ft] |
| DMT-AR+CM 400x300 | 0.0703 m² | 379 mm | 759 m³/h | 253 m³/h | 300 mm | 285 mm  [stored 0.935039 ft] | 31.7 mm | 300 mm | -0.86996 | 400 mm  [stored 1.31234 ft] | 385 mm | DMT-AR+CM 400x300 | 8 | 11 | 400x300 | 400 mm  [stored 1.31234 ft] |
| DMT-AR+CM 400x250 | 0.0580 m² | 379 mm | 626 m³/h | 209 m³/h | 250 mm  [stored 0.82021 ft] | 235 mm  [stored 0.770997 ft] | 33.6 mm | 250 mm  [stored 0.82021 ft] | -1.701776 | 400 mm  [stored 1.31234 ft] | 385 mm | DMT-AR+CM 400x250 | 6 | 9 | 400x250 | 400 mm  [stored 1.31234 ft] |
| DMT-AR+CM 400x200 | 0.0457 m² | 379 mm | 493 m³/h | 164 m³/h | 200 mm  [stored 0.656168 ft] | 185 mm  [stored 0.606955 ft] | 30.8 mm | 200 mm  [stored 0.656168 ft] | -2.732688 | 400 mm  [stored 1.31234 ft] | 385 mm | DMT-AR+CM 400x200 | 5 | 7 | 400x200 | 400 mm  [stored 1.31234 ft] |
| DMT-AR+CM 400x150 | 0.0334 m² | 379 mm | 361 m³/h | 120 m³/h | 150 mm | 135 mm  [stored 0.442913 ft] | 27 mm  [stored 0.0885827 ft] | 150 mm | -4.089023 | 400 mm  [stored 1.31234 ft] | 385 mm | DMT-AR+CM 400x150 | 4 | 5 | 400x150 | 400 mm  [stored 1.31234 ft] |
| DMT-AR+CM 400x100 | 0.0211 m² | 379 mm | 228 m³/h | 76 m³/h | 100 mm  [stored 0.328084 ft] | 85 mm  [stored 0.278871 ft] | 21.3 mm | 100 mm  [stored 0.328084 ft] | -6.076302 | 400 mm  [stored 1.31234 ft] | 385 mm | DMT-AR+CM 400x100 | 3 | 3 | 400x100 | 400 mm  [stored 1.31234 ft] |
| EMT-AR+CM 1000x350 | 0.2110 m² | 329 mm | 2,279 m³/h | 760 m³/h | 1000 mm | 985 mm | 37.9 mm | 1000 mm | 3.882295 | 350 mm  [stored 1.14829 ft] | 335 mm | EMT-AR+CM 1000x350 | 25 | 39 | 350x1000 | 350 mm  [stored 1.14829 ft] |
| EMT-AR+CM 900x350 | 0.1896 m² | 329 mm | 2,048 m³/h | 683 m³/h | 900 mm | 885 mm | 36.9 mm | 900 mm | 3.419867 | 350 mm  [stored 1.14829 ft] | 335 mm | EMT-AR+CM 900x350 | 23 | 35 | 350x900 | 350 mm  [stored 1.14829 ft] |
| EMT-AR+CM 800x350 | 0.1682 m² | 329 mm | 1,817 m³/h | 606 m³/h | 800 mm | 785 mm | 37.4 mm | 800 mm | 2.901991 | 350 mm  [stored 1.14829 ft] | 335 mm | DMT-AR+CM 350x800 | 20 | 31 | 350x800 | 350 mm  [stored 1.14829 ft] |
| EMT-AR+CM 700x350 | 0.1468 m² | 329 mm | 1,585 m³/h | 528 m³/h | 700 mm | 685 mm | 36.1 mm | 700 mm | 2.313535 | 350 mm  [stored 1.14829 ft] | 335 mm | EMT-AR+CM 700x350 | 18 | 27 | 350x700 | 350 mm  [stored 1.14829 ft] |
| EMT-AR+CM 600x350 | 0.1254 m² | 329 mm | 1,354 m³/h | 451 m³/h | 600 mm | 585 mm | 36.6 mm | 600 mm | 1.632178 | 350 mm  [stored 1.14829 ft] | 335 mm | EMT-AR+CM 600x350 | 15 | 23 | 350x600 | 350 mm  [stored 1.14829 ft] |
| EMT-AR+CM 500x350 | 0.1040 m² | 329 mm | 1,123 m³/h | 374 m³/h | 500 mm | 485 mm | 34.6 mm | 500 mm | 0.822987 | 350 mm  [stored 1.14829 ft] | 335 mm | EMT-AR+CM 500x350 | 13 | 19 | 350x500 | 350 mm  [stored 1.14829 ft] |
| EMT-AR+CM 450x350 | 0.0933 m² | 329 mm | 1,008 m³/h | 336 m³/h | 450 mm  [stored 1.47638 ft] | 435 mm | 36.3 mm | 450 mm  [stored 1.47638 ft] | 0.353456 | 350 mm  [stored 1.14829 ft] | 335 mm | EMT-AR+CM 450x350 | 11 | 17 | 350x450 | 350 mm  [stored 1.14829 ft] |
| EMT-AR+CM 400x350 | 0.0826 m² | 329 mm | 892 m³/h | 297 m³/h | 400 mm  [stored 1.31234 ft] | 385 mm | 35 mm  [stored 0.114829 ft] | 400 mm  [stored 1.31234 ft] | -0.173346 | 350 mm  [stored 1.14829 ft] | 335 mm | EMT-AR+CM 400x350 | 10 | 15 | 350x400 | 350 mm  [stored 1.14829 ft] |
| DMT-AR+CM 350x350 | 0.0719 m² | 329 mm | 776 m³/h | 259 m³/h | 350 mm  [stored 1.14829 ft] | 335 mm | 33.5 mm | 350 mm  [stored 1.14829 ft] | -0.77336 | 350 mm  [stored 1.14829 ft] | 335 mm | DMT-AR+CM 350x350 | 9 | 13 | 350x350 | 350 mm  [stored 1.14829 ft] |
| DMT-AR+CM 350x300 | 0.0612 m² | 329 mm | 661 m³/h | 220 m³/h | 300 mm | 285 mm  [stored 0.935039 ft] | 31.7 mm | 300 mm | -1.470268 | 350 mm  [stored 1.14829 ft] | 335 mm | DMT-AR+CM 350x300 | 8 | 11 | 350x300 | 350 mm  [stored 1.14829 ft] |
| DMT-AR+CM 350x250 | 0.0505 m² | 329 mm | 545 m³/h | 182 m³/h | 250 mm  [stored 0.82021 ft] | 235 mm  [stored 0.770997 ft] | 33.6 mm | 250 mm  [stored 0.82021 ft] | -2.301508 | 350 mm  [stored 1.14829 ft] | 335 mm | DMT-AR+CM 350x250 | 6 | 9 | 350x250 | 350 mm  [stored 1.14829 ft] |
| DMT-AR+CM 350x200 | 0.0398 m² | 329 mm | 430 m³/h | 143 m³/h | 200 mm  [stored 0.656168 ft] | 185 mm  [stored 0.606955 ft] | 30.8 mm | 200 mm  [stored 0.656168 ft] | -3.331533 | 350 mm  [stored 1.14829 ft] | 335 mm | DMT-AR+CM 350x200 | 5 | 7 | 350x200 | 350 mm  [stored 1.14829 ft] |
| DMT-AR+CM 350x150 | 0.0291 m² | 329 mm | 314 m³/h | 105 m³/h | 150 mm | 135 mm  [stored 0.442913 ft] | 27 mm  [stored 0.0885827 ft] | 150 mm | -4.686329 | 350 mm  [stored 1.14829 ft] | 335 mm | DMT-AR+CM 350x150 | 4 | 5 | 350x150 | 350 mm  [stored 1.14829 ft] |
| DMT-AR+CM 350x100 | 0.0184 m² | 329 mm | 199 m³/h | 66 m³/h | 100 mm  [stored 0.328084 ft] | 85 mm  [stored 0.278871 ft] | 21.3 mm | 100 mm  [stored 0.328084 ft] | -6.670274 | 350 mm  [stored 1.14829 ft] | 335 mm | DMT-AR+CM 350x100 | 3 | 3 | 350x100 | 350 mm  [stored 1.14829 ft] |
| EMT-AR+CM 1000x300 | 0.1795 m² | 279 mm | 1,938 m³/h | 646 m³/h | 1000 mm | 985 mm | 37.9 mm | 1000 mm | 3.182382 | 300 mm | 285 mm  [stored 0.935039 ft] | EMT-AR+CM 1000x300 | 25 | 39 | 300x1000 | 300 mm |
| EMT-AR+CM 900x300 | 0.1613 m² | 279 mm | 1,742 m³/h | 581 m³/h | 900 mm | 885 mm | 36.9 mm | 900 mm | 2.720074 | 300 mm | 285 mm  [stored 0.935039 ft] | EMT-AR+CM 900x300 | 23 | 35 | 300x900 | 300 mm |
| EMT-AR+CM 800x300 | 0.1431 m² | 279 mm | 1,545 m³/h | 515 m³/h | 800 mm | 785 mm | 37.4 mm | 800 mm | 2.20235 | 300 mm | 285 mm  [stored 0.935039 ft] | EMT-AR+CM 800x300 | 20 | 31 | 300x800 | 300 mm |
| EMT-AR+CM 700x300 | 0.1249 m² | 279 mm | 1,349 m³/h | 450 m³/h | 700 mm | 685 mm | 36.1 mm | 700 mm | 1.614088 | 300 mm | 285 mm  [stored 0.935039 ft] | EMT-AR+CM 700x300 | 18 | 27 | 300x700 | 300 mm |
| EMT-AR+CM 600x300 | 0.1067 m² | 279 mm | 1,152 m³/h | 384 m³/h | 600 mm | 585 mm | 36.6 mm | 600 mm | 0.932992 | 300 mm | 285 mm  [stored 0.935039 ft] | EMT-AR+CM 600x300 | 15 | 23 | 300x600 | 300 mm |
| EMT-AR+CM 500x300 | 0.0885 m² | 279 mm | 956 m³/h | 319 m³/h | 500 mm | 485 mm | 34.6 mm | 500 mm | 0.12417 | 300 mm | 285 mm  [stored 0.935039 ft] | EMT-AR+CM 500x300 | 13 | 19 | 300x500 | 300 mm |
| EMT-AR+CM 450x300 | 0.0794 m² | 279 mm | 857 m³/h | 286 m³/h | 450 mm  [stored 1.47638 ft] | 435 mm | 36.3 mm | 450 mm  [stored 1.47638 ft] | -0.345113 | 300 mm | 285 mm  [stored 0.935039 ft] | EMT-AR+CM 450x300 | 11 | 17 | 300x450 | 300 mm |
| EMT-AR+CM 400x300 | 0.0703 m² | 279 mm | 759 m³/h | 253 m³/h | 400 mm  [stored 1.31234 ft] | 385 mm | 35 mm  [stored 0.114829 ft] | 400 mm  [stored 1.31234 ft] | -0.871603 | 300 mm | 285 mm  [stored 0.935039 ft] | EMT-AR+CM 400x300 | 10 | 15 | 300x400 | 300 mm |
| EMT-AR+CM 350x300 | 0.0612 m² | 279 mm | 661 m³/h | 220 m³/h | 350 mm  [stored 1.14829 ft] | 335 mm | 33.5 mm | 350 mm  [stored 1.14829 ft] | -1.471212 | 300 mm | 285 mm  [stored 0.935039 ft] | EMT-AR+CM 350x300 | 9 | 13 | 300x350 | 300 mm |
| DMT-AR+CM 300x300 | 0.0521 m² | 279 mm | 562 m³/h | 187 m³/h | 300 mm | 285 mm  [stored 0.935039 ft] | 31.7 mm | 300 mm | -2.167574 | 300 mm | 285 mm  [stored 0.935039 ft] | DMT-AR+CM 300x300 | 8 | 11 | 300x300 | 300 mm |
| DMT-AR+CM 300x250 | 0.0430 m² | 279 mm | 464 m³/h | 155 m³/h | 250 mm  [stored 0.82021 ft] | 235 mm  [stored 0.770997 ft] | 33.6 mm | 250 mm  [stored 0.82021 ft] | -2.998036 | 300 mm | 285 mm  [stored 0.935039 ft] | DMT-AR+CM 300x250 | 6 | 9 | 300x250 | 300 mm |
| DMT-AR+CM 300x200 | 0.0339 m² | 279 mm | 366 m³/h | 122 m³/h | 200 mm  [stored 0.656168 ft] | 185 mm  [stored 0.606955 ft] | 30.8 mm | 200 mm  [stored 0.656168 ft] | -4.026865 | 300 mm | 285 mm  [stored 0.935039 ft] | DMT-AR+CM 300x200 | 5 | 7 | 300x200 | 300 mm |
| DMT-AR+CM 300x150 | 0.0248 m² | 279 mm | 268 m³/h | 89 m³/h | 150 mm | 135 mm  [stored 0.442913 ft] | 27 mm  [stored 0.0885827 ft] | 150 mm | -5.379586 | 300 mm | 285 mm  [stored 0.935039 ft] | DMT-AR+CM 300x150 | 4 | 5 | 300x150 | 300 mm |
| DMT-AR+CM 300x100 | 0.0157 m² | 279 mm | 169 m³/h | 56 m³/h | 100 mm  [stored 0.328084 ft] | 85 mm  [stored 0.278871 ft] | 21.3 mm | 100 mm  [stored 0.328084 ft] | -7.359041 | 300 mm | 285 mm  [stored 0.935039 ft] | DMT-AR+CM 300x100 | 3 | 3 | 300x100 | 300 mm |
| EMT-AR+CM 1000x250 | 0.1479 m² | 229 mm | 1,598 m³/h | 533 m³/h | 1000 mm | 985 mm | 37.9 mm | 1000 mm | 2.34686 | 250 mm  [stored 0.82021 ft] | 235 mm  [stored 0.770997 ft] | EMT-AR+CM 1000x250 | 25 | 39 | 250x1000 | 250 mm  [stored 0.82021 ft] |
| EMT-AR+CM 900x250 | 0.1329 m² | 229 mm | 1,436 m³/h | 479 m³/h | 900 mm | 885 mm | 36.9 mm | 900 mm | 1.884724 | 250 mm  [stored 0.82021 ft] | 235 mm  [stored 0.770997 ft] | EMT-AR+CM 900x250 | 23 | 35 | 250x900 | 250 mm  [stored 0.82021 ft] |
| EMT-AR+CM 800x250 | 0.1179 m² | 229 mm | 1,274 m³/h | 425 m³/h | 800 mm | 785 mm | 37.4 mm | 800 mm | 1.367215 | 250 mm  [stored 0.82021 ft] | 235 mm  [stored 0.770997 ft] | EMT-AR+CM 800x250 | 20 | 31 | 250x800 | 250 mm  [stored 0.82021 ft] |
| EMT-AR+CM 700x250 | 0.1029 m² | 229 mm | 1,112 m³/h | 371 m³/h | 700 mm | 685 mm | 36.1 mm | 700 mm | 0.779231 | 250 mm  [stored 0.82021 ft] | 235 mm  [stored 0.770997 ft] | EMT-AR+CM 700x250 | 18 | 27 | 250x700 | 250 mm  [stored 0.82021 ft] |
| EMT-AR+CM 600x250 | 0.0880 m² | 229 mm | 950 m³/h | 317 m³/h | 600 mm | 585 mm | 36.6 mm | 600 mm | 0.098508 | 250 mm  [stored 0.82021 ft] | 235 mm  [stored 0.770997 ft] | EMT-AR+CM 600x250 | 15 | 23 | 250x600 | 250 mm  [stored 0.82021 ft] |
| EMT-AR+CM 500x250 | 0.0730 m² | 229 mm | 788 m³/h | 263 m³/h | 500 mm | 485 mm | 34.6 mm | 500 mm | -0.709789 | 250 mm  [stored 0.82021 ft] | 235 mm  [stored 0.770997 ft] | EMT-AR+CM 500x250 | 13 | 19 | 250x500 | 250 mm  [stored 0.82021 ft] |
| EMT-AR+CM 450x250 | 0.0655 m² | 229 mm | 707 m³/h | 236 m³/h | 450 mm  [stored 1.47638 ft] | 435 mm | 36.3 mm | 450 mm  [stored 1.47638 ft] | -1.178719 | 250 mm  [stored 0.82021 ft] | 235 mm  [stored 0.770997 ft] | EMT-AR+CM 450x250 | 11 | 17 | 250x450 | 250 mm  [stored 0.82021 ft] |
| EMT-AR+CM 400x250 | 0.0580 m² | 229 mm | 626 m³/h | 209 m³/h | 400 mm  [stored 1.31234 ft] | 385 mm | 35 mm  [stored 0.114829 ft] | 400 mm  [stored 1.31234 ft] | -1.704765 | 250 mm  [stored 0.82021 ft] | 235 mm  [stored 0.770997 ft] | EMT-AR+CM 400x250 | 10 | 15 | 250x400 | 250 mm  [stored 0.82021 ft] |
| EMT-AR+CM 350x250 | 0.0505 m² | 229 mm | 545 m³/h | 182 m³/h | 350 mm  [stored 1.14829 ft] | 335 mm | 33.5 mm | 350 mm  [stored 1.14829 ft] | -2.303797 | 250 mm  [stored 0.82021 ft] | 235 mm  [stored 0.770997 ft] | EMT-AR+CM 350x250 | 9 | 13 | 250x350 | 250 mm  [stored 0.82021 ft] |
| EMT-AR+CM 300x250 | 0.0430 m² | 229 mm | 464 m³/h | 155 m³/h | 300 mm | 285 mm  [stored 0.935039 ft] | 31.7 mm | 300 mm | -2.99938 | 250 mm  [stored 0.82021 ft] | 235 mm  [stored 0.770997 ft] | EMT-AR+CM 300x250 | 8 | 11 | 250x300 | 250 mm  [stored 0.82021 ft] |
| DMT-AR+CM 250x250 | 0.0355 m² | 229 mm | 383 m³/h | 128 m³/h | 250 mm  [stored 0.82021 ft] | 235 mm  [stored 0.770997 ft] | 33.6 mm | 250 mm  [stored 0.82021 ft] | -3.828735 | 250 mm  [stored 0.82021 ft] | 235 mm  [stored 0.770997 ft] | DMT-AR+CM 250x250 | 6 | 9 | 250x250 | 250 mm  [stored 0.82021 ft] |
| DMT-AR+CM 250x200 | 0.0280 m² | 229 mm | 302 m³/h | 101 m³/h | 200 mm  [stored 0.656168 ft] | 185 mm  [stored 0.606955 ft] | 30.8 mm | 200 mm  [stored 0.656168 ft] | -4.855862 | 250 mm  [stored 0.82021 ft] | 235 mm  [stored 0.770997 ft] | DMT-AR+CM 250x200 | 5 | 7 | 250x200 | 250 mm  [stored 0.82021 ft] |
| DMT-AR+CM 250x150 | 0.0205 m² | 229 mm | 221 m³/h | 74 m³/h | 150 mm | 135 mm  [stored 0.442913 ft] | 27 mm  [stored 0.0885827 ft] | 150 mm | -6.205631 | 250 mm  [stored 0.82021 ft] | 235 mm  [stored 0.770997 ft] | DMT-AR+CM 250x150 | 4 | 5 | 250x150 | 250 mm  [stored 0.82021 ft] |
| DMT-AR+CM 250x100 | 0.0130 m² | 229 mm | 140 m³/h | 47 m³/h | 100 mm  [stored 0.328084 ft] | 85 mm  [stored 0.278871 ft] | 21.3 mm | 100 mm  [stored 0.328084 ft] | -8.178715 | 250 mm  [stored 0.82021 ft] | 235 mm  [stored 0.770997 ft] | DMT-AR+CM 250x100 | 3 | 3 | 250x100 | 250 mm  [stored 0.82021 ft] |
| EMT-AR+CM 1000x200 | 0.1164 m² | 179 mm  [stored 0.58727 ft] | 1,257 m³/h | 419 m³/h | 1000 mm | 985 mm | 37.9 mm | 1000 mm | 1.310241 | 200 mm  [stored 0.656168 ft] | 185 mm  [stored 0.606955 ft] | EMT-AR+CM 1000x200 | 25 | 39 | 200x1000 | 200 mm  [stored 0.656168 ft] |
| EMT-AR+CM 900x200 | 0.1046 m² | 179 mm  [stored 0.58727 ft] | 1,130 m³/h | 377 m³/h | 900 mm | 885 mm | 36.9 mm | 900 mm | 0.848369 | 200 mm  [stored 0.656168 ft] | 185 mm  [stored 0.606955 ft] | EMT-AR+CM 900x200 | 23 | 35 | 200x900 | 200 mm  [stored 0.656168 ft] |
| EMT-AR+CM 800x200 | 0.0928 m² | 179 mm  [stored 0.58727 ft] | 1,002 m³/h | 334 m³/h | 800 mm | 785 mm | 37.4 mm | 800 mm | 0.331191 | 200 mm  [stored 0.656168 ft] | 185 mm  [stored 0.606955 ft] | EMT-AR+CM 800x200 | 20 | 31 | 200x800 | 200 mm  [stored 0.656168 ft] |
| EMT-AR+CM 700x200 | 0.0810 m² | 179 mm  [stored 0.58727 ft] | 875 m³/h | 292 m³/h | 700 mm | 685 mm | 36.1 mm | 700 mm | -0.256365 | 200 mm  [stored 0.656168 ft] | 185 mm  [stored 0.606955 ft] | EMT-AR+CM 700x200 | 18 | 27 | 200x700 | 200 mm  [stored 0.656168 ft] |
| EMT-AR+CM 600x200 | 0.0692 m² | 179 mm  [stored 0.58727 ft] | 748 m³/h | 249 m³/h | 600 mm | 585 mm | 36.6 mm | 600 mm | -0.936514 | 200 mm  [stored 0.656168 ft] | 185 mm  [stored 0.606955 ft] | EMT-AR+CM 600x200 | 15 | 23 | 200x600 | 200 mm  [stored 0.656168 ft] |
| EMT-AR+CM 500x200 | 0.0574 m² | 179 mm  [stored 0.58727 ft] | 620 m³/h | 207 m³/h | 500 mm | 485 mm | 34.6 mm | 500 mm | -1.744001 | 200 mm  [stored 0.656168 ft] | 185 mm  [stored 0.606955 ft] | EMT-AR+CM 500x200 | 13 | 19 | 200x500 | 200 mm  [stored 0.656168 ft] |
| EMT-AR+CM 450x200 | 0.0515 m² | 179 mm  [stored 0.58727 ft] | 557 m³/h | 186 m³/h | 450 mm  [stored 1.47638 ft] | 435 mm | 36.3 mm | 450 mm  [stored 1.47638 ft] | -2.212386 | 200 mm  [stored 0.656168 ft] | 185 mm  [stored 0.606955 ft] | EMT-AR+CM 450x200 | 11 | 17 | 200x450 | 200 mm  [stored 0.656168 ft] |
| EMT-AR+CM 400x200 | 0.0456 m² | 179 mm  [stored 0.58727 ft] | 493 m³/h | 164 m³/h | 400 mm  [stored 1.31234 ft] | 385 mm | 35 mm  [stored 0.114829 ft] | 400 mm  [stored 1.31234 ft] | -2.737748 | 200 mm  [stored 0.656168 ft] | 185 mm  [stored 0.606955 ft] | EMT-AR+CM 400x200 | 10 | 15 | 200x400 | 200 mm  [stored 0.656168 ft] |
| EMT-AR+CM 350x200 | 0.0397 m² | 179 mm  [stored 0.58727 ft] | 429 m³/h | 143 m³/h | 350 mm  [stored 1.14829 ft] | 335 mm | 33.5 mm | 350 mm  [stored 1.14829 ft] | -3.335892 | 200 mm  [stored 0.656168 ft] | 185 mm  [stored 0.606955 ft] | EMT-AR+CM 350x200 | 9 | 13 | 200x350 | 200 mm  [stored 0.656168 ft] |
| EMT-AR+CM 300x200 | 0.0338 m² | 179 mm  [stored 0.58727 ft] | 366 m³/h | 122 m³/h | 300 mm | 285 mm  [stored 0.935039 ft] | 31.7 mm | 300 mm | -4.030278 | 200 mm  [stored 0.656168 ft] | 185 mm  [stored 0.606955 ft] | EMT-AR+CM 300x200 | 8 | 11 | 200x300 | 200 mm  [stored 0.656168 ft] |
| EMT-AR+CM 250x200 | 0.0280 m² | 179 mm  [stored 0.58727 ft] | 302 m³/h | 101 m³/h | 250 mm  [stored 0.82021 ft] | 235 mm  [stored 0.770997 ft] | 33.6 mm | 250 mm  [stored 0.82021 ft] | -4.857928 | 200 mm  [stored 0.656168 ft] | 185 mm  [stored 0.606955 ft] | EMT-AR+CM 250x200 | 6 | 9 | 200x250 | 200 mm  [stored 0.656168 ft] |
| DMT-AR+CM 200x200 | 0.0221 m² | 179 mm  [stored 0.58727 ft] | 238 m³/h | 79 m³/h | 200 mm  [stored 0.656168 ft] | 185 mm  [stored 0.606955 ft] | 30.8 mm | 200 mm  [stored 0.656168 ft] | -5.882439 | 200 mm  [stored 0.656168 ft] | 185 mm  [stored 0.606955 ft] | DMT-AR+CM 200x200 | 5 | 7 | 200x200 | 200 mm  [stored 0.656168 ft] |
| DMT-AR+CM 200x150 | 0.0162 m² | 179 mm  [stored 0.58727 ft] | 174 m³/h | 58 m³/h | 150 mm | 135 mm  [stored 0.442913 ft] | 27 mm  [stored 0.0885827 ft] | 150 mm | -7.227679 | 200 mm  [stored 0.656168 ft] | 185 mm  [stored 0.606955 ft] | DMT-AR+CM 200x150 | 4 | 5 | 200x150 | 200 mm  [stored 0.656168 ft] |
| DMT-AR+CM 200x100 | 0.0103 m² | 179 mm  [stored 0.58727 ft] | 111 m³/h | 37 m³/h | 100 mm  [stored 0.328084 ft] | 85 mm  [stored 0.278871 ft] | 21.3 mm | 100 mm  [stored 0.328084 ft] | -9.191011 | 200 mm  [stored 0.656168 ft] | 185 mm  [stored 0.606955 ft] | DMT-AR+CM 200x100 | 3 | 3 | 200x100 | 200 mm  [stored 0.656168 ft] |
| EMT-AR+CM 1000x150 | 0.0849 m² | 129 mm  [stored 0.423228 ft] | 917 m³/h | 306 m³/h | 1000 mm | 985 mm | 37.9 mm | 1000 mm | -0.056025 | 150 mm | 135 mm  [stored 0.442913 ft] | EMT-AR+CM 1000x150 | 25 | 39 | 150x1000 | 150 mm |
| EMT-AR+CM 900x150 | 0.0763 m² | 129 mm  [stored 0.423228 ft] | 824 m³/h | 275 m³/h | 900 mm | 885 mm | 36.9 mm | 900 mm | -0.517436 | 150 mm | 135 mm  [stored 0.442913 ft] | EMT-AR+CM 900x150 | 23 | 35 | 150x900 | 150 mm |
| EMT-AR+CM 800x150 | 0.0677 m² | 129 mm  [stored 0.423228 ft] | 731 m³/h | 244 m³/h | 800 mm | 785 mm | 37.4 mm | 800 mm | -1.034037 | 150 mm | 135 mm  [stored 0.442913 ft] | EMT-AR+CM 800x150 | 20 | 31 | 150x800 | 150 mm |
| EMT-AR+CM 700x150 | 0.0591 m² | 129 mm  [stored 0.423228 ft] | 638 m³/h | 213 m³/h | 700 mm | 685 mm | 36.1 mm | 700 mm | -1.620847 | 150 mm | 135 mm  [stored 0.442913 ft] | EMT-AR+CM 700x150 | 18 | 27 | 150x700 | 150 mm |
| EMT-AR+CM 600x150 | 0.0505 m² | 129 mm  [stored 0.423228 ft] | 545 m³/h | 182 m³/h | 600 mm | 585 mm | 36.6 mm | 600 mm | -2.299996 | 150 mm | 135 mm  [stored 0.442913 ft] | EMT-AR+CM 600x150 | 15 | 23 | 150x600 | 150 mm |
| EMT-AR+CM 500x150 | 0.0419 m² | 129 mm  [stored 0.423228 ft] | 453 m³/h | 151 m³/h | 500 mm | 485 mm | 34.6 mm | 500 mm | -3.106073 | 150 mm | 135 mm  [stored 0.442913 ft] | EMT-AR+CM 500x150 | 13 | 19 | 150x500 | 150 mm |
| EMT-AR+CM 450x150 | 0.0376 m² | 129 mm  [stored 0.423228 ft] | 406 m³/h | 135 m³/h | 450 mm  [stored 1.47638 ft] | 435 mm | 36.3 mm | 450 mm  [stored 1.47638 ft] | -3.573512 | 150 mm | 135 mm  [stored 0.442913 ft] | EMT-AR+CM 450x150 | 11 | 17 | 150x450 | 150 mm |
| EMT-AR+CM 400x150 | 0.0333 m² | 129 mm  [stored 0.423228 ft] | 360 m³/h | 120 m³/h | 400 mm  [stored 1.31234 ft] | 385 mm | 35 mm  [stored 0.114829 ft] | 400 mm  [stored 1.31234 ft] | -4.097682 | 150 mm | 135 mm  [stored 0.442913 ft] | EMT-AR+CM 400x150 | 10 | 15 | 150x400 | 150 mm |
| EMT-AR+CM 350x150 | 0.0290 m² | 129 mm  [stored 0.423228 ft] | 314 m³/h | 105 m³/h | 350 mm  [stored 1.14829 ft] | 335 mm | 33.5 mm | 350 mm  [stored 1.14829 ft] | -4.694282 | 150 mm | 135 mm  [stored 0.442913 ft] | EMT-AR+CM 350x150 | 9 | 13 | 150x350 | 150 mm |
| EMT-AR+CM 300x150 | 0.0247 m² | 129 mm  [stored 0.423228 ft] | 267 m³/h | 89 m³/h | 300 mm | 285 mm  [stored 0.935039 ft] | 31.7 mm | 300 mm | -5.386587 | 150 mm | 135 mm  [stored 0.442913 ft] | EMT-AR+CM 300x150 | 8 | 11 | 150x300 | 150 mm |
| EMT-AR+CM 250x150 | 0.0204 m² | 129 mm  [stored 0.423228 ft] | 221 m³/h | 74 m³/h | 250 mm  [stored 0.82021 ft] | 235 mm  [stored 0.770997 ft] | 33.6 mm | 250 mm  [stored 0.82021 ft] | -6.21128 | 150 mm | 135 mm  [stored 0.442913 ft] | EMT-AR+CM 250x150 | 6 | 9 | 150x250 | 150 mm |
| EMT-AR+CM 200x150 | 0.0161 m² | 129 mm  [stored 0.423228 ft] | 174 m³/h | 58 m³/h | 200 mm  [stored 0.656168 ft] | 185 mm  [stored 0.606955 ft] | 30.8 mm | 200 mm  [stored 0.656168 ft] | -7.231256 | 150 mm | 135 mm  [stored 0.442913 ft] | EMT-AR+CM 200x150 | 5 | 7 | 150x200 | 150 mm |
| DMT-AR+CM 150x150 | 0.0118 m² | 129 mm  [stored 0.423228 ft] | 128 m³/h | 43 m³/h | 150 mm | 135 mm  [stored 0.442913 ft] | 27 mm  [stored 0.0885827 ft] | 150 mm | -8.568661 | 150 mm | 135 mm  [stored 0.442913 ft] | DMT-AR+CM 150x150 | 4 | 5 | 150x150 | 150 mm |
| DMT-AR+CM 150x100 | 0.0076 m² | 129 mm  [stored 0.423228 ft] | 82 m³/h | 27 m³/h | 100 mm  [stored 0.328084 ft] | 85 mm  [stored 0.278871 ft] | 21.3 mm | 100 mm  [stored 0.328084 ft] | -10.515201 | 150 mm | 135 mm  [stored 0.442913 ft] | DMT-AR+CM 150x100 | 3 | 3 | 150x100 | 150 mm |
| EMT-AR+CM 1000x100 | 0.0533 m² | 79 mm  [stored 0.259186 ft] | 576 m³/h | 192 m³/h | 1000 mm | 985 mm | 37.9 mm | 1000 mm | -2.064904 | 100 mm  [stored 0.328084 ft] | 85 mm  [stored 0.278871 ft] | EMT-AR+CM 1000x100 | 25 | 39 | 100x1000 | 100 mm  [stored 0.328084 ft] |
| EMT-AR+CM 900x100 | 0.0479 m² | 79 mm  [stored 0.259186 ft] | 518 m³/h | 173 m³/h | 900 mm | 885 mm | 36.9 mm | 900 mm | -2.525309 | 100 mm  [stored 0.328084 ft] | 85 mm  [stored 0.278871 ft] | EMT-AR+CM 900x100 | 23 | 35 | 100x900 | 100 mm  [stored 0.328084 ft] |
| EMT-AR+CM 800x100 | 0.0426 m² | 79 mm  [stored 0.259186 ft] | 460 m³/h | 153 m³/h | 800 mm | 785 mm | 37.4 mm | 800 mm | -3.040649 | 100 mm  [stored 0.328084 ft] | 85 mm  [stored 0.278871 ft] | EMT-AR+CM 800x100 | 20 | 31 | 100x800 | 100 mm  [stored 0.328084 ft] |
| EMT-AR+CM 700x100 | 0.0372 m² | 79 mm  [stored 0.259186 ft] | 401 m³/h | 134 m³/h | 700 mm | 685 mm | 36.1 mm | 700 mm | -3.625833 | 100 mm  [stored 0.328084 ft] | 85 mm  [stored 0.278871 ft] | EMT-AR+CM 700x100 | 18 | 27 | 100x700 | 100 mm  [stored 0.328084 ft] |
| EMT-AR+CM 600x100 | 0.0318 m² | 79 mm  [stored 0.259186 ft] | 343 m³/h | 114 m³/h | 600 mm | 585 mm | 36.6 mm | 600 mm | -4.302804 | 100 mm  [stored 0.328084 ft] | 85 mm  [stored 0.278871 ft] | EMT-AR+CM 600x100 | 15 | 23 | 100x600 | 100 mm  [stored 0.328084 ft] |
| EMT-AR+CM 500x100 | 0.0264 m² | 79 mm  [stored 0.259186 ft] | 285 m³/h | 95 m³/h | 500 mm | 485 mm | 34.6 mm | 500 mm | -5.105811 | 100 mm  [stored 0.328084 ft] | 85 mm  [stored 0.278871 ft] | EMT-AR+CM 500x100 | 13 | 19 | 100x500 | 100 mm  [stored 0.328084 ft] |
| EMT-AR+CM 450x100 | 0.0237 m² | 79 mm  [stored 0.259186 ft] | 256 m³/h | 85 m³/h | 450 mm  [stored 1.47638 ft] | 435 mm | 36.3 mm | 450 mm  [stored 1.47638 ft] | -5.57119 | 100 mm  [stored 0.328084 ft] | 85 mm  [stored 0.278871 ft] | EMT-AR+CM 450x100 | 11 | 17 | 100x450 | 100 mm  [stored 0.328084 ft] |
| EMT-AR+CM 400x100 | 0.0210 m² | 79 mm  [stored 0.259186 ft] | 227 m³/h | 76 m³/h | 400 mm  [stored 1.31234 ft] | 385 mm | 35 mm  [stored 0.114829 ft] | 400 mm  [stored 1.31234 ft] | -6.092771 | 100 mm  [stored 0.328084 ft] | 85 mm  [stored 0.278871 ft] | EMT-AR+CM 400x100 | 10 | 15 | 100x400 | 100 mm  [stored 0.328084 ft] |
| EMT-AR+CM 350x100 | 0.0183 m² | 79 mm  [stored 0.259186 ft] | 198 m³/h | 66 m³/h | 350 mm  [stored 1.14829 ft] | 335 mm | 33.5 mm | 350 mm  [stored 1.14829 ft] | -6.686018 | 100 mm  [stored 0.328084 ft] | 85 mm  [stored 0.278871 ft] | EMT-AR+CM 350x100 | 9 | 13 | 100x350 | 100 mm  [stored 0.328084 ft] |
| EMT-AR+CM 300x100 | 0.0156 m² | 79 mm  [stored 0.259186 ft] | 169 m³/h | 56 m³/h | 300 mm | 285 mm  [stored 0.935039 ft] | 31.7 mm | 300 mm | -7.37381 | 100 mm  [stored 0.328084 ft] | 85 mm  [stored 0.278871 ft] | EMT-AR+CM 300x100 | 8 | 11 | 100x300 | 100 mm  [stored 0.328084 ft] |
| EMT-AR+CM 250x100 | 0.0129 m² | 79 mm  [stored 0.259186 ft] | 140 m³/h | 47 m³/h | 250 mm  [stored 0.82021 ft] | 235 mm  [stored 0.770997 ft] | 33.6 mm | 250 mm  [stored 0.82021 ft] | -8.192101 | 100 mm  [stored 0.328084 ft] | 85 mm  [stored 0.278871 ft] | EMT-AR+CM 250x100 | 6 | 9 | 100x250 | 100 mm  [stored 0.328084 ft] |
| EMT-AR+CM 200x100 | 0.0102 m² | 79 mm  [stored 0.259186 ft] | 111 m³/h | 37 m³/h | 200 mm  [stored 0.656168 ft] | 185 mm  [stored 0.606955 ft] | 30.8 mm | 200 mm  [stored 0.656168 ft] | -9.202287 | 100 mm  [stored 0.328084 ft] | 85 mm  [stored 0.278871 ft] | EMT-AR+CM 200x100 | 5 | 7 | 100x200 | 100 mm  [stored 0.328084 ft] |
| EMT-AR+CM 150x100 | 0.0075 m² | 79 mm  [stored 0.259186 ft] | 81 m³/h | 27 m³/h | 150 mm | 135 mm  [stored 0.442913 ft] | 27 mm  [stored 0.0885827 ft] | 150 mm | -10.522856 | 100 mm  [stored 0.328084 ft] | 85 mm  [stored 0.278871 ft] | EMT-AR+CM 150x100 | 4 | 5 | 100x150 | 100 mm  [stored 0.328084 ft] |
| DMT-AR+CM 100x100 | 0.0048 m² | 79 mm  [stored 0.259186 ft] | 52 m³/h | 17 m³/h | 100 mm  [stored 0.328084 ft] | 85 mm  [stored 0.278871 ft] | 21.3 mm | 100 mm  [stored 0.328084 ft] | -12.43363 | 100 mm  [stored 0.328084 ft] | 85 mm  [stored 0.278871 ft] | DMT-AR+CM 100x100 | 3 | 3 | 100x100 | 100 mm  [stored 0.328084 ft] |

note: [stored X ft] marks values corroborated as IEEE doubles in the binary element streams (Revit-internal decimal feet)

## geometry (parser evidence)
native form markers: Blend x2
no freeform markers — native parametric forms only
